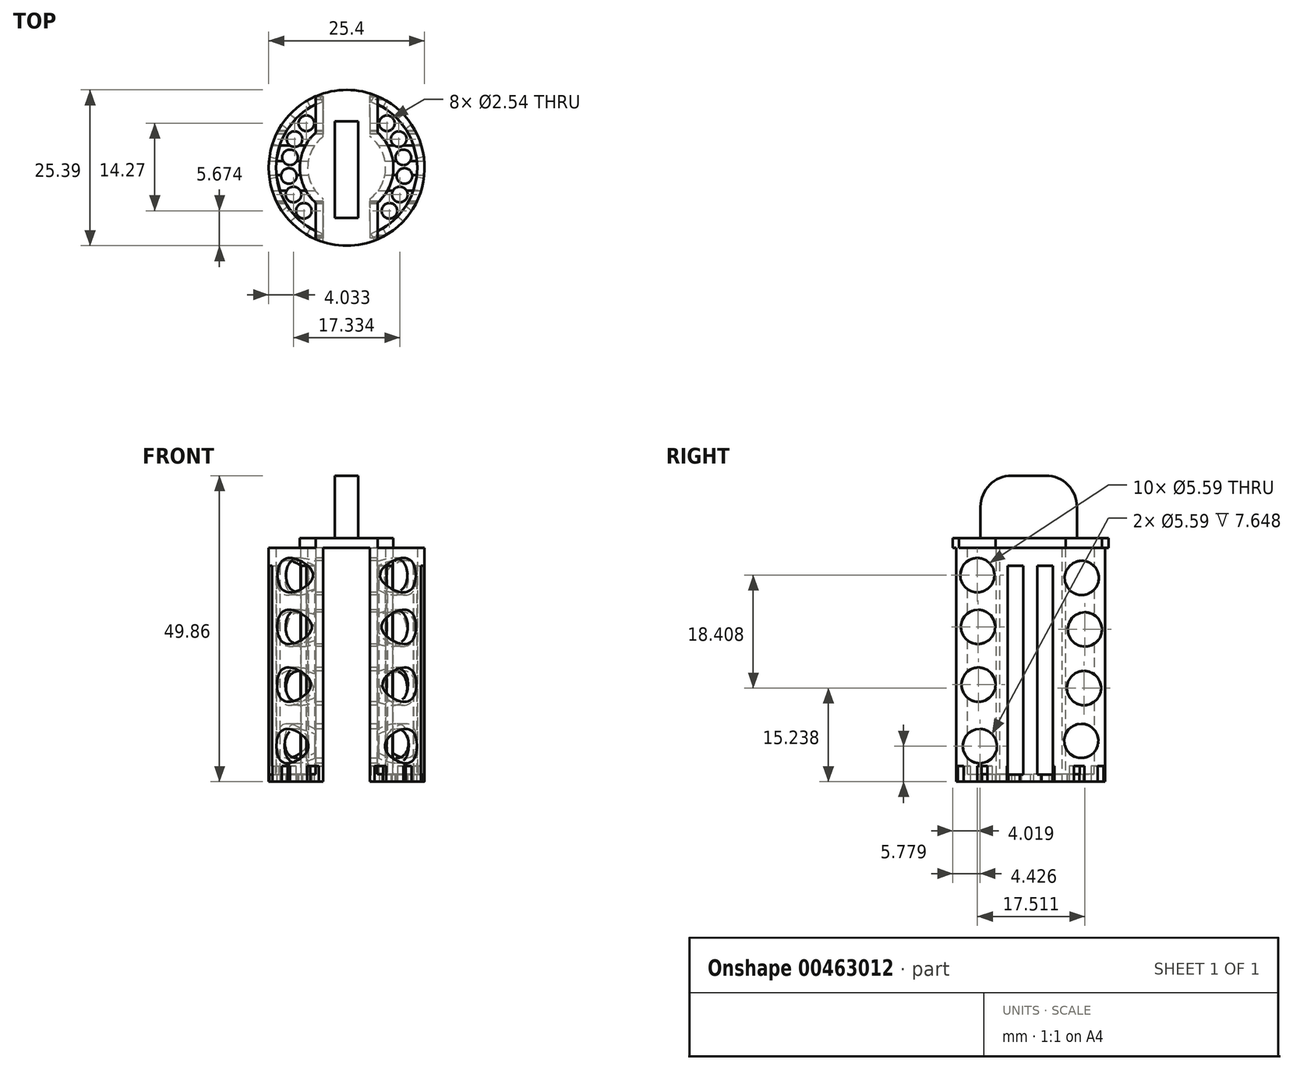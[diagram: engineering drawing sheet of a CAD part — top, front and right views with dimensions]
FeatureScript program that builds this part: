
annotation { "Feature Type Name" : "Feature", "Feature Type Description" : "" }
export const myFeature = defineFeature(function(context is Context, id is Id, definition is map)
    precondition{}
    {
        {
            var Q0;
            Q0=qCreatedBy(makeId("Top.planeOp"),FACE);
            var sketch = newSketch(context, id + "F0", { "sketchPlane" : qUnion([Q0])});
            skArc(sketch, "E0", {"start": v(3.81, -12.12) * mm, "mid": v(12.7, 0) * mm, "end": v(3.8, 12.12) * mm});
            skLineSegment(sketch, "E1", {"start": v(3.8, 12.12) * mm, "end": v(3.8, 5.08) * mm});
            skLineSegment(sketch, "E2", {"start": v(-3.8, -12.12) * mm, "end": v(-3.8, -5.08) * mm});
            skArc(sketch, "E3", {"start": v(-3.81, 5.08) * mm, "mid": v(-6.35, 0) * mm, "end": v(-3.81, -5.08) * mm});
            skLineSegment(sketch, "E4.trimOffspring", {"start": v(-3.81, 5.08) * mm, "end": v(-3.81, 12.12) * mm});
            skLineSegment(sketch, "E5.trimOffspring", {"start": v(3.81, -5.08) * mm, "end": v(3.81, -12.12) * mm});
            skArc(sketch, "E6.trimOffspring", {"start": v(3.81, -5.08) * mm, "mid": v(6.35, 0) * mm, "end": v(3.81, 5.08) * mm});
            skArc(sketch, "E7.trimOffspring", {"start": v(-3.8, 12.12) * mm, "mid": v(-12.7, 0) * mm, "end": v(-3.81, -12.12) * mm});
            skSolve(sketch);
        }
        {
            var Q0;
            Q0 = qSketchRegion(id + "F0", true);
            extrude(context, id + "F1", {"entities" : qUnion([Q0]), "depth" : 38.1 * mm});
        }
        {
            var Q0;
            Q0=makeQuery(id+"F1.opExtrude","CAP_FACE",FACE,{"disambiguationData":[OSD([sQuery(id+"F0.wireOp",EDGE,"E2"),sQuery(id+"F0.wireOp",EDGE,"E3"),sQuery(id+"F0.wireOp",EDGE,"E4.trimOffspring"),sQuery(id+"F0.wireOp",EDGE,"E7.trimOffspring")])],"isStart":false});
            var Q1;
            Q1=makeQuery(id+"F1.opExtrude","CAP_FACE",FACE,{"disambiguationData":[OSD([sQuery(id+"F0.wireOp",EDGE,"E0"),sQuery(id+"F0.wireOp",EDGE,"E1"),sQuery(id+"F0.wireOp",EDGE,"E5.trimOffspring"),sQuery(id+"F0.wireOp",EDGE,"E6.trimOffspring")])],"isStart":false});
            shell(context, id + "F2", {"entities" : qUnion([Q0, Q1]), "thickness" : 1.2 * mm});
        }
        {
            var Q0;
            Q0=makeQuery(id+"F1.opExtrude","CAP_FACE",FACE,{"disambiguationData":[OSD([sQuery(id+"F0.wireOp",EDGE,"E2"),sQuery(id+"F0.wireOp",EDGE,"E3"),sQuery(id+"F0.wireOp",EDGE,"E4.trimOffspring"),sQuery(id+"F0.wireOp",EDGE,"E7.trimOffspring")])],"isStart":false});
            var sketch = newSketch(context, id + "F3", { "sketchPlane" : qUnion([Q0])});
            skArc(sketch, "E8", {"start": v(-5.01, 5.75) * mm, "mid": v(-7.63, 0) * mm, "end": v(-5, -5.75) * mm});
            skLineSegment(sketch, "E9", {"start": v(-5.01, 5.65) * mm, "end": v(-5.01, 11.67) * mm});
            skLineSegment(sketch, "E10", {"start": v(-5, -5.65) * mm, "end": v(-5, -11.67) * mm});
            skLineSegment(sketch, "E11", {"start": v(5.05, -5.72) * mm, "end": v(5.05, -11.67) * mm});
            skLineSegment(sketch, "E12", {"start": v(5.05, 5.72) * mm, "end": v(5.05, 11.64) * mm});
            skArc(sketch, "E13", {"start": v(-5, -11.67) * mm, "mid": v(0.02, -12.7) * mm, "end": v(5.05, -11.65) * mm});
            skArc(sketch, "E14.trimOffspring", {"start": v(5.05, 11.64) * mm, "mid": v(0.02, 12.7) * mm, "end": v(-5, 11.66) * mm});
            skArc(sketch, "E15.trimOffspring", {"start": v(5.05, -5.72) * mm, "mid": v(7.63, 0) * mm, "end": v(5.05, 5.72) * mm});
            skSolve(sketch);
        }
        {
            var Q0;
            Q0 = qSketchRegion(id + "F3", true);
            extrude(context, id + "F4", {"entities" : qUnion([Q0]), "operationType" : NewBodyOperationType.ADD, "depth" : 1.6 * mm});
        }
        {
            var Q0;
            Q0=makeQuery(id+"F1.opExtrude","CAP_FACE",FACE,{"disambiguationData":[OSD([sQuery(id+"F0.wireOp",EDGE,"E0"),sQuery(id+"F0.wireOp",EDGE,"E1"),sQuery(id+"F0.wireOp",EDGE,"E5.trimOffspring"),sQuery(id+"F0.wireOp",EDGE,"E6.trimOffspring")])],"isStart":true});
            var sketch = newSketch(context, id + "F5", { "sketchPlane" : qUnion([Q0])});
            skCircle(sketch, "E16", {"center": v(-6.97, 7.03) * mm, "radius": 1.27 * mm});
            skCircle(sketch, "E17", {"center": v(-8.67, 4.36) * mm, "radius": 1.27 * mm});
            skCircle(sketch, "E18", {"center": v(-9.41, 1.34) * mm, "radius": 1.27 * mm});
            skCircle(sketch, "E19", {"center": v(-6.56, -7.24) * mm, "radius": 1.27 * mm});
            skCircle(sketch, "E20", {"center": v(-9.24, -1.7) * mm, "radius": 1.27 * mm});
            skCircle(sketch, "E21", {"center": v(-8.5, -4.67) * mm, "radius": 1.27 * mm});
            skLineSegment(sketch, "E22", {"start": v(0, -0.53) * mm, "end": v(0, 3.55) * mm});
            skCircle(sketch, "E23.MirrorC", {"center": v(6.56, -7.24) * mm, "radius": 1.27 * mm});
            skCircle(sketch, "E24.MirrorC", {"center": v(8.5, -4.67) * mm, "radius": 1.27 * mm});
            skCircle(sketch, "E25.MirrorC", {"center": v(9.24, -1.7) * mm, "radius": 1.27 * mm});
            skCircle(sketch, "E26.MirrorC", {"center": v(9.41, 1.34) * mm, "radius": 1.27 * mm});
            skCircle(sketch, "E27.MirrorC", {"center": v(8.67, 4.36) * mm, "radius": 1.27 * mm});
            skCircle(sketch, "E28.MirrorC", {"center": v(6.97, 7.03) * mm, "radius": 1.27 * mm});
            skSolve(sketch);
        }
        {
            var Q0;
            Q0 = qSketchRegion(id + "F5", true);
            extrude(context, id + "F6", {"entities" : qUnion([Q0]), "operationType" : NewBodyOperationType.REMOVE, "oppositeDirection" : true, "depth" : 25.4 * mm});
        }
        {
            var Q0;
            Q0=makeQuery(id+"F1.opExtrude","SWEPT_FACE",FACE,{"disambiguationData":[OSD([sQuery(id+"F0.wireOp",EDGE,"E5.trimOffspring")])]});
            var sketch = newSketch(context, id + "F7", { "sketchPlane" : qUnion([Q0])});
            skCircle(sketch, "E29", {"center": v(8.27, 5.78) * mm, "radius": 2.8 * mm});
            skCircle(sketch, "E30", {"center": v(8.5, 15.8) * mm, "radius": 2.8 * mm});
            skCircle(sketch, "E31", {"center": v(8.57, 25.21) * mm, "radius": 2.8 * mm});
            skCircle(sketch, "E32", {"center": v(8.68, 33.65) * mm, "radius": 2.8 * mm});
            skCircle(sketch, "E33", {"center": v(-8.25, 6.63) * mm, "radius": 2.8 * mm});
            skCircle(sketch, "E34", {"center": v(-8.7, 15.24) * mm, "radius": 2.8 * mm});
            skCircle(sketch, "E35", {"center": v(-8.83, 24.8) * mm, "radius": 2.8 * mm});
            skCircle(sketch, "E36", {"center": v(-8.32, 33.2) * mm, "radius": 2.8 * mm});
            skSolve(sketch);
        }
        {
            var Q0;
            Q0 = qSketchRegion(id + "F7", true);
            extrude(context, id + "F8", {"entities" : qUnion([Q0]), "operationType" : NewBodyOperationType.REMOVE, "oppositeDirection" : true, "depth" : 25.4 * mm, "hasSecondDirection" : true, "secondDirectionOppositeDirection" : false, "secondDirectionDepth" : 25.4 * mm});
        }
        {
            var Q0;
            Q0=qCreatedBy(makeId("Right.planeOp"),FACE);
            var sketch = newSketch(context, id + "F9", { "sketchPlane" : qUnion([Q0])});
            skLineSegment(sketch, "E37.bottom", {"start": v(-3.77, 35.18) * mm, "end": v(-1.23, 35.18) * mm});
            skLineSegment(sketch, "E37.top", {"start": v(-3.77, 1.11) * mm, "end": v(-1.23, 1.11) * mm});
            skLineSegment(sketch, "E37.left", {"start": v(-3.77, 35.18) * mm, "end": v(-3.77, 1.11) * mm});
            skLineSegment(sketch, "E37.right", {"start": v(-1.23, 35.18) * mm, "end": v(-1.23, 1.11) * mm});
            skLineSegment(sketch, "E38.bottom", {"start": v(1.08, 35.18) * mm, "end": v(3.62, 35.18) * mm});
            skLineSegment(sketch, "E38.top", {"start": v(1.08, 1.15) * mm, "end": v(3.62, 1.15) * mm});
            skLineSegment(sketch, "E38.left", {"start": v(1.08, 35.18) * mm, "end": v(1.08, 1.15) * mm});
            skLineSegment(sketch, "E38.right", {"start": v(3.62, 35.18) * mm, "end": v(3.62, 1.15) * mm});
            skSolve(sketch);
        }
        {
            var Q0;
            Q0 = qSketchRegion(id + "F9", true);
            extrude(context, id + "F10", {"entities" : qUnion([Q0]), "operationType" : NewBodyOperationType.REMOVE, "oppositeDirection" : true, "depth" : 25.4 * mm, "hasSecondDirection" : true, "secondDirectionOppositeDirection" : false, "secondDirectionDepth" : 25.4 * mm});
        }
        {
            var Q0;
            Q0=makeQuery(id+"F1.opExtrude","CAP_FACE",FACE,{"disambiguationData":[OSD([sQuery(id+"F0.wireOp",EDGE,"E2"),sQuery(id+"F0.wireOp",EDGE,"E3"),sQuery(id+"F0.wireOp",EDGE,"E4.trimOffspring"),sQuery(id+"F0.wireOp",EDGE,"E7.trimOffspring")])],"isStart":true});
            var sketch = newSketch(context, id + "F11", { "sketchPlane" : qUnion([Q0])});
            skLineSegment(sketch, "E39.bottom", {"start": v(1.08, 13.94) * mm, "end": v(-1.08, 13.94) * mm});
            skLineSegment(sketch, "E39.top", {"start": v(1.08, 11.43) * mm, "end": v(-1.08, 11.43) * mm});
            skLineSegment(sketch, "E39.left", {"start": v(1.08, 13.94) * mm, "end": v(1.08, 11.43) * mm});
            skLineSegment(sketch, "E39.right", {"start": v(-1.08, 13.94) * mm, "end": v(-1.08, 11.43) * mm});
            skPoint(sketch, "E39.middle", {"position": v(0, 12.68) * mm});
            skLineSegment(sketch, "E40.1.0", {"start": v(-5.08, 13.02) * mm, "end": v(-7.02, 12.1) * mm});
            skLineSegment(sketch, "E40.1.1", {"start": v(-7.02, 12.1) * mm, "end": v(-5.93, 9.83) * mm});
            skLineSegment(sketch, "E40.1.2", {"start": v(-3.99, 10.76) * mm, "end": v(-5.93, 9.83) * mm});
            skLineSegment(sketch, "E40.1.3", {"start": v(-5.08, 13.02) * mm, "end": v(-3.99, 10.76) * mm});
            skLineSegment(sketch, "E40.2.0", {"start": v(-10.23, 9.53) * mm, "end": v(-11.57, 7.85) * mm});
            skLineSegment(sketch, "E40.2.1", {"start": v(-11.57, 7.85) * mm, "end": v(-9.6, 6.28) * mm});
            skLineSegment(sketch, "E40.2.2", {"start": v(-8.26, 7.97) * mm, "end": v(-9.6, 6.28) * mm});
            skLineSegment(sketch, "E40.2.3", {"start": v(-10.23, 9.53) * mm, "end": v(-8.26, 7.97) * mm});
            skLineSegment(sketch, "E40.3.0", {"start": v(-13.35, 4.15) * mm, "end": v(-13.83, 2.05) * mm});
            skLineSegment(sketch, "E40.3.1", {"start": v(-13.83, 2.05) * mm, "end": v(-11.38, 1.5) * mm});
            skLineSegment(sketch, "E40.3.2", {"start": v(-10.9, 3.6) * mm, "end": v(-11.38, 1.5) * mm});
            skLineSegment(sketch, "E40.3.3", {"start": v(-13.35, 4.15) * mm, "end": v(-10.9, 3.6) * mm});
            skLineSegment(sketch, "E40.4.0", {"start": v(-13.83, -2.05) * mm, "end": v(-13.35, -4.15) * mm});
            skLineSegment(sketch, "E40.4.1", {"start": v(-13.35, -4.15) * mm, "end": v(-10.9, -3.6) * mm});
            skLineSegment(sketch, "E40.4.2", {"start": v(-11.38, -1.5) * mm, "end": v(-10.9, -3.6) * mm});
            skLineSegment(sketch, "E40.4.3", {"start": v(-13.83, -2.05) * mm, "end": v(-11.38, -1.5) * mm});
            skLineSegment(sketch, "E40.5.0", {"start": v(-11.57, -7.85) * mm, "end": v(-10.23, -9.53) * mm});
            skLineSegment(sketch, "E40.5.1", {"start": v(-10.23, -9.53) * mm, "end": v(-8.26, -7.97) * mm});
            skLineSegment(sketch, "E40.5.2", {"start": v(-9.6, -6.28) * mm, "end": v(-8.26, -7.97) * mm});
            skLineSegment(sketch, "E40.5.3", {"start": v(-11.57, -7.85) * mm, "end": v(-9.6, -6.28) * mm});
            skLineSegment(sketch, "E40.6.0", {"start": v(-7.02, -12.1) * mm, "end": v(-5.08, -13.02) * mm});
            skLineSegment(sketch, "E40.6.1", {"start": v(-5.08, -13.02) * mm, "end": v(-3.99, -10.76) * mm});
            skLineSegment(sketch, "E40.6.2", {"start": v(-5.93, -9.83) * mm, "end": v(-3.99, -10.76) * mm});
            skLineSegment(sketch, "E40.6.3", {"start": v(-7.02, -12.1) * mm, "end": v(-5.93, -9.83) * mm});
            skLineSegment(sketch, "E40.7.0", {"start": v(-1.08, -13.94) * mm, "end": v(1.08, -13.94) * mm});
            skLineSegment(sketch, "E40.7.1", {"start": v(1.08, -13.94) * mm, "end": v(1.08, -11.43) * mm});
            skLineSegment(sketch, "E40.7.2", {"start": v(-1.08, -11.43) * mm, "end": v(1.08, -11.43) * mm});
            skLineSegment(sketch, "E40.7.3", {"start": v(-1.08, -13.94) * mm, "end": v(-1.08, -11.43) * mm});
            skLineSegment(sketch, "E40.8.0", {"start": v(5.08, -13.02) * mm, "end": v(7.02, -12.1) * mm});
            skLineSegment(sketch, "E40.8.1", {"start": v(7.02, -12.1) * mm, "end": v(5.93, -9.83) * mm});
            skLineSegment(sketch, "E40.8.2", {"start": v(3.99, -10.76) * mm, "end": v(5.93, -9.83) * mm});
            skLineSegment(sketch, "E40.8.3", {"start": v(5.08, -13.02) * mm, "end": v(3.99, -10.76) * mm});
            skLineSegment(sketch, "E40.9.0", {"start": v(10.23, -9.53) * mm, "end": v(11.57, -7.85) * mm});
            skLineSegment(sketch, "E40.9.1", {"start": v(11.57, -7.85) * mm, "end": v(9.6, -6.28) * mm});
            skLineSegment(sketch, "E40.9.2", {"start": v(8.26, -7.97) * mm, "end": v(9.6, -6.28) * mm});
            skLineSegment(sketch, "E40.9.3", {"start": v(10.23, -9.53) * mm, "end": v(8.26, -7.97) * mm});
            skLineSegment(sketch, "E40.10.0", {"start": v(13.35, -4.15) * mm, "end": v(13.83, -2.05) * mm});
            skLineSegment(sketch, "E40.10.1", {"start": v(13.83, -2.05) * mm, "end": v(11.38, -1.5) * mm});
            skLineSegment(sketch, "E40.10.2", {"start": v(10.9, -3.6) * mm, "end": v(11.38, -1.5) * mm});
            skLineSegment(sketch, "E40.10.3", {"start": v(13.35, -4.15) * mm, "end": v(10.9, -3.6) * mm});
            skLineSegment(sketch, "E40.11.0", {"start": v(13.83, 2.05) * mm, "end": v(13.35, 4.15) * mm});
            skLineSegment(sketch, "E40.11.1", {"start": v(13.35, 4.15) * mm, "end": v(10.9, 3.6) * mm});
            skLineSegment(sketch, "E40.11.2", {"start": v(11.38, 1.5) * mm, "end": v(10.9, 3.6) * mm});
            skLineSegment(sketch, "E40.11.3", {"start": v(13.83, 2.05) * mm, "end": v(11.38, 1.5) * mm});
            skLineSegment(sketch, "E40.12.0", {"start": v(11.57, 7.85) * mm, "end": v(10.23, 9.53) * mm});
            skLineSegment(sketch, "E40.12.1", {"start": v(10.23, 9.53) * mm, "end": v(8.26, 7.97) * mm});
            skLineSegment(sketch, "E40.12.2", {"start": v(9.6, 6.28) * mm, "end": v(8.26, 7.97) * mm});
            skLineSegment(sketch, "E40.12.3", {"start": v(11.57, 7.85) * mm, "end": v(9.6, 6.28) * mm});
            skLineSegment(sketch, "E40.13.0", {"start": v(7.02, 12.1) * mm, "end": v(5.08, 13.02) * mm});
            skLineSegment(sketch, "E40.13.1", {"start": v(5.08, 13.02) * mm, "end": v(3.99, 10.76) * mm});
            skLineSegment(sketch, "E40.13.2", {"start": v(5.93, 9.83) * mm, "end": v(3.99, 10.76) * mm});
            skLineSegment(sketch, "E40.13.3", {"start": v(7.02, 12.1) * mm, "end": v(5.93, 9.83) * mm});
            skPoint(sketch, "E40.center", {"position": v(0, 0) * mm});
            skSolve(sketch);
        }
        {
            var Q0;
            Q0=makeQuery(id+"F11.imprint","IMPRINT",FACE,{"disambiguationData":[TD([[makeQuery(id+"F11.imprint","IMPRINT",EDGE,{"derivedFrom":sQuery(id+"F11.wireOp",EDGE,"E40.12.0")}),1.0]])]});
            var Q1;
            Q1=makeQuery(id+"F11.imprint","IMPRINT",FACE,{"disambiguationData":[TD([[makeQuery(id+"F11.imprint","IMPRINT",EDGE,{"derivedFrom":sQuery(id+"F11.wireOp",EDGE,"E40.13.0")}),1.0]])]});
            var Q2;
            Q2=makeQuery(id+"F11.imprint","IMPRINT",FACE,{"disambiguationData":[TD([[makeQuery(id+"F11.imprint","IMPRINT",EDGE,{"derivedFrom":sQuery(id+"F11.wireOp",EDGE,"E39.bottom")}),1.0]])]});
            var Q3;
            {var subQ0=sQuery(id+"F11.wireOp",EDGE,"E40.1.0");Q3=makeQuery(id+"F11.imprint","IMPRINT",FACE,{"disambiguationData":[TD([[makeQuery(id+"F11.imprint","IMPRINT",EDGE,{"derivedFrom":subQ0}),1.0]])]});}
            var Q4;
            {var subQ0=sQuery(id+"F11.wireOp",EDGE,"E40.2.0");Q4=makeQuery(id+"F11.imprint","IMPRINT",FACE,{"disambiguationData":[TD([[makeQuery(id+"F11.imprint","IMPRINT",EDGE,{"derivedFrom":subQ0}),1.0]])]});}
            var Q5;
            {var subQ0=sQuery(id+"F11.wireOp",EDGE,"E40.3.2");Q5=makeQuery(id+"F11.imprint","IMPRINT",FACE,{"disambiguationData":[TD([[makeQuery(id+"F11.imprint","IMPRINT",EDGE,{"derivedFrom":subQ0}),-1.0]])]});}
            var Q6;
            {var subQ0=sQuery(id+"F11.wireOp",EDGE,"E40.2.2");Q6=makeQuery(id+"F11.imprint","IMPRINT",FACE,{"disambiguationData":[TD([[makeQuery(id+"F11.imprint","IMPRINT",EDGE,{"derivedFrom":subQ0}),-1.0]])]});}
            var Q7;
            {var subQ0=sQuery(id+"F11.wireOp",EDGE,"E40.1.2");Q7=makeQuery(id+"F11.imprint","IMPRINT",FACE,{"disambiguationData":[TD([[makeQuery(id+"F11.imprint","IMPRINT",EDGE,{"derivedFrom":subQ0}),-1.0]])]});}
            var Q8;
            Q8=makeQuery(id+"F11.imprint","IMPRINT",FACE,{"disambiguationData":[TD([[makeQuery(id+"F11.imprint","IMPRINT",EDGE,{"derivedFrom":sQuery(id+"F11.wireOp",EDGE,"E40.11.0")}),1.0]])]});
            var Q9;
            Q9=makeQuery(id+"F11.imprint","IMPRINT",FACE,{"disambiguationData":[TD([[makeQuery(id+"F11.imprint","IMPRINT",EDGE,{"derivedFrom":sQuery(id+"F11.wireOp",EDGE,"E40.10.0")}),1.0]])]});
            var Q10;
            Q10=makeQuery(id+"F11.imprint","IMPRINT",FACE,{"disambiguationData":[TD([[makeQuery(id+"F11.imprint","IMPRINT",EDGE,{"derivedFrom":sQuery(id+"F11.wireOp",EDGE,"E40.9.0")}),1.0]])]});
            var Q11;
            Q11=makeQuery(id+"F11.imprint","IMPRINT",FACE,{"disambiguationData":[TD([[makeQuery(id+"F11.imprint","IMPRINT",EDGE,{"derivedFrom":sQuery(id+"F11.wireOp",EDGE,"E40.8.0")}),1.0]])]});
            var Q12;
            Q12=makeQuery(id+"F11.imprint","IMPRINT",FACE,{"disambiguationData":[TD([[makeQuery(id+"F11.imprint","IMPRINT",EDGE,{"derivedFrom":sQuery(id+"F11.wireOp",EDGE,"E40.7.0")}),1.0]])]});
            var Q13;
            {var subQ0=sQuery(id+"F11.wireOp",EDGE,"E40.6.2");Q13=makeQuery(id+"F11.imprint","IMPRINT",FACE,{"disambiguationData":[TD([[makeQuery(id+"F11.imprint","IMPRINT",EDGE,{"derivedFrom":subQ0}),-1.0]])]});}
            var Q14;
            {var subQ0=sQuery(id+"F11.wireOp",EDGE,"E40.5.2");Q14=makeQuery(id+"F11.imprint","IMPRINT",FACE,{"disambiguationData":[TD([[makeQuery(id+"F11.imprint","IMPRINT",EDGE,{"derivedFrom":subQ0}),-1.0]])]});}
            var Q15;
            {var subQ0=sQuery(id+"F11.wireOp",EDGE,"E40.4.2");Q15=makeQuery(id+"F11.imprint","IMPRINT",FACE,{"disambiguationData":[TD([[makeQuery(id+"F11.imprint","IMPRINT",EDGE,{"derivedFrom":subQ0}),-1.0]])]});}
            extrude(context, id + "F12", {"entities" : qUnion([Q0, Q1, Q2, Q3, Q4, Q5, Q6, Q7, Q8, Q9, Q10, Q11, Q12, Q13, Q14, Q15]), "operationType" : NewBodyOperationType.REMOVE, "oppositeDirection" : true, "depth" : 2.54 * mm});
        }
        {
            var Q0;
            Q0=makeQuery(id+"F4.opExtrude","CAP_FACE",FACE,{"disambiguationData":[OSD([sQuery(id+"F3.wireOp",EDGE,"E8"),sQuery(id+"F3.wireOp",EDGE,"E9"),sQuery(id+"F3.wireOp",EDGE,"E10"),sQuery(id+"F3.wireOp",EDGE,"E11"),sQuery(id+"F3.wireOp",EDGE,"E12"),sQuery(id+"F3.wireOp",EDGE,"E13"),sQuery(id+"F3.wireOp",EDGE,"E14.trimOffspring"),sQuery(id+"F3.wireOp",EDGE,"E15.trimOffspring")])],"isStart":false});
            var sketch = newSketch(context, id + "F13", { "sketchPlane" : qUnion([Q0])});
            skLineSegment(sketch, "E41.bottom", {"start": v(-1.9, 7.55) * mm, "end": v(1.9, 7.55) * mm});
            skLineSegment(sketch, "E41.top", {"start": v(-1.9, -8.17) * mm, "end": v(1.9, -8.17) * mm});
            skLineSegment(sketch, "E41.left", {"start": v(-1.9, 7.55) * mm, "end": v(-1.9, -8.17) * mm});
            skLineSegment(sketch, "E41.right", {"start": v(1.9, 7.55) * mm, "end": v(1.9, -8.17) * mm});
            skSolve(sketch);
        }
        {
            var Q0;
            Q0=makeQuery(id+"F13.imprint","IMPRINT",FACE,{"disambiguationData":[TD([[makeQuery(id+"F13.imprint","IMPRINT",EDGE,{"derivedFrom":sQuery(id+"F13.wireOp",EDGE,"E41.bottom")}),-1.0]])]});
            var Q1;
            Q1=sQuery(id+"F13.wireOp",EDGE,"E41.right");
            var Q2;
            Q2=sQuery(id+"F13.wireOp",EDGE,"E41.bottom");
            var Q3;
            Q3=sQuery(id+"F13.wireOp",EDGE,"E41.left");
            var Q4;
            Q4=sQuery(id+"F13.wireOp",EDGE,"E41.top");
            extrude(context, id + "F14", {"entities" : qUnion([Q0]), "operationType" : NewBodyOperationType.ADD, "surfaceEntities" : qUnion([Q1, Q2, Q3, Q4]), "depth" : 10.16 * mm});
        }
        {
            var Q0;
            Q0=makeQuery(id+"F14.opExtrude","CAP_EDGE",EDGE,{"disambiguationData":[OSD([sQuery(id+"F13.wireOp",EDGE,"E41.bottom")])],"isStart":false});
            var Q1;
            Q1=makeQuery(id+"F14.opExtrude","CAP_EDGE",EDGE,{"disambiguationData":[OSD([sQuery(id+"F13.wireOp",EDGE,"E41.top")])],"isStart":false});
            fillet(context, id + "F15", {"entities" : qUnion([Q0, Q1]), "radius" : 5.08 * mm, "tangentPropagation" : true, "allowEdgeOverflow" : false});
        }
    });
